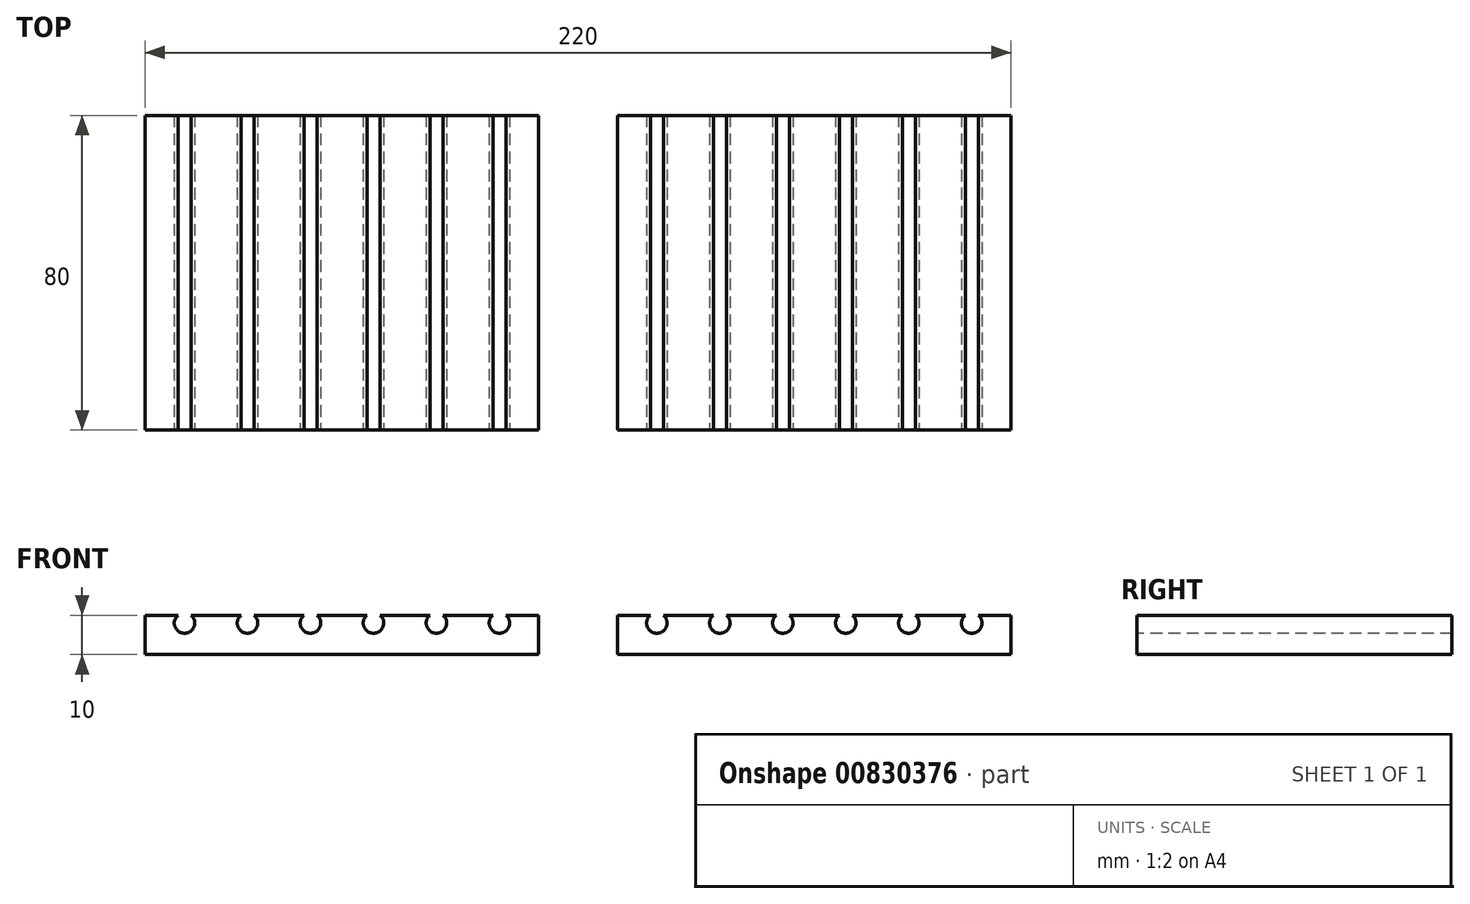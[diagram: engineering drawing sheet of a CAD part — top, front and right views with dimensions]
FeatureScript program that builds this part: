
annotation { "Feature Type Name" : "Feature", "Feature Type Description" : "" }
export const myFeature = defineFeature(function(context is Context, id is Id, definition is map)
    precondition{}
    {
        {
            var Q0;
            Q0=qCreatedBy(makeId("Top.planeOp"),FACE);
            var sketch = newSketch(context, id + "F0", { "sketchPlane" : qUnion([Q0])});
            skLineSegment(sketch, "E0.bottom", {"start": v(50, 40) * mm, "end": v(-50, 40) * mm});
            skLineSegment(sketch, "E0.top", {"start": v(50, -40) * mm, "end": v(-50, -40) * mm});
            skLineSegment(sketch, "E0.left", {"start": v(50, 40) * mm, "end": v(50, -40) * mm});
            skLineSegment(sketch, "E0.right", {"start": v(-50, 40) * mm, "end": v(-50, -40) * mm});
            skPoint(sketch, "E0.middle", {"position": v(0, 0) * mm});
            skSolve(sketch);
        }
        {
            var Q0;
            Q0=makeQuery(id+"F0.imprint","IMPRINT",FACE,{"disambiguationData":[TD([[makeQuery(id+"F0.imprint","IMPRINT",EDGE,{"derivedFrom":sQuery(id+"F0.wireOp",EDGE,"E0.bottom")}),1.0]])]});
            extrude(context, id + "F1", {"entities" : qUnion([Q0]), "depth" : 10 * mm, "offsetDistance" : 25 * mm});
        }
        {
            var Q0;
            Q0=makeQuery(id+"F1.opExtrude","SWEPT_FACE",FACE,{"disambiguationData":[OSD([sQuery(id+"F0.wireOp",EDGE,"E0.top")])]});
            var sketch = newSketch(context, id + "F2", { "sketchPlane" : qUnion([Q0])});
            skLineSegment(sketch, "E1.0.0", {"start": v(-50, 0) * mm, "end": v(50, 0) * mm});
            skLineSegment(sketch, "E1.0.1", {"start": v(50, 0) * mm, "end": v(50, 10) * mm});
            skLineSegment(sketch, "E1.0.2", {"start": v(50, 10) * mm, "end": v(-50, 10) * mm});
            skLineSegment(sketch, "E1.0.3", {"start": v(-50, 10) * mm, "end": v(-50, 0) * mm});
            skLineSegment(sketch, "E2", {"start": v(-50, 8) * mm, "end": v(50, 8) * mm, "construction": true});
            skCircle(sketch, "E3", {"center": v(-40, 8) * mm, "radius": 2.6 * mm});
            skCircle(sketch, "E4.1.0.0", {"center": v(-24, 8) * mm, "radius": 2.6 * mm});
            skCircle(sketch, "E4.2.0.0", {"center": v(-8, 8) * mm, "radius": 2.6 * mm});
            skCircle(sketch, "E4.3.0.0", {"center": v(8, 8) * mm, "radius": 2.6 * mm});
            skCircle(sketch, "E4.4.0.0", {"center": v(24, 8) * mm, "radius": 2.6 * mm});
            skCircle(sketch, "E4.5.0.0", {"center": v(40, 8) * mm, "radius": 2.6 * mm});
            skLineSegment(sketch, "E4.direction1", {"start": v(-40, 8) * mm, "end": v(-24, 8) * mm, "construction": true});
            skSolve(sketch);
        }
        {
            var Q0;
            {var subQ0=sQuery(id+"F2.wireOp",EDGE,"E4.5.0.0");var subQ1=sQuery(id+"F2.wireOp",EDGE,"E1.0.2");var subQ2=makeQuery(id+"F2.imprint","INTERSECT",VERTEX,{"disambiguationData":[OD(0.0)],"derivedFrom":[subQ1,subQ0]});Q0=makeQuery(id+"F2.imprint","IMPRINT",FACE,{"disambiguationData":[TD([[makeQuery(id+"F2.imprint","IMPRINT",EDGE,{"disambiguationData":[TD([[subQ2,-1.0]])],"derivedFrom":subQ1}),-1.0]])]});}
            var Q1;
            {var subQ0=sQuery(id+"F2.wireOp",EDGE,"E4.4.0.0");var subQ1=sQuery(id+"F2.wireOp",EDGE,"E1.0.2");var subQ2=makeQuery(id+"F2.imprint","INTERSECT",VERTEX,{"disambiguationData":[OD(0.0)],"derivedFrom":[subQ1,subQ0]});Q1=makeQuery(id+"F2.imprint","IMPRINT",FACE,{"disambiguationData":[TD([[makeQuery(id+"F2.imprint","IMPRINT",EDGE,{"disambiguationData":[TD([[subQ2,-1.0]])],"derivedFrom":subQ1}),-1.0]])]});}
            var Q2;
            {var subQ0=sQuery(id+"F2.wireOp",EDGE,"E4.3.0.0");var subQ1=sQuery(id+"F2.wireOp",EDGE,"E1.0.2");var subQ2=makeQuery(id+"F2.imprint","INTERSECT",VERTEX,{"disambiguationData":[OD(0.0)],"derivedFrom":[subQ1,subQ0]});Q2=makeQuery(id+"F2.imprint","IMPRINT",FACE,{"disambiguationData":[TD([[makeQuery(id+"F2.imprint","IMPRINT",EDGE,{"disambiguationData":[TD([[subQ2,-1.0]])],"derivedFrom":subQ1}),-1.0]])]});}
            var Q3;
            {var subQ0=sQuery(id+"F2.wireOp",EDGE,"E4.2.0.0");var subQ1=sQuery(id+"F2.wireOp",EDGE,"E1.0.2");var subQ2=makeQuery(id+"F2.imprint","INTERSECT",VERTEX,{"disambiguationData":[OD(0.0)],"derivedFrom":[subQ1,subQ0]});Q3=makeQuery(id+"F2.imprint","IMPRINT",FACE,{"disambiguationData":[TD([[makeQuery(id+"F2.imprint","IMPRINT",EDGE,{"disambiguationData":[TD([[subQ2,-1.0]])],"derivedFrom":subQ1}),-1.0]])]});}
            var Q4;
            {var subQ0=sQuery(id+"F2.wireOp",EDGE,"E4.1.0.0");var subQ1=sQuery(id+"F2.wireOp",EDGE,"E1.0.2");var subQ2=makeQuery(id+"F2.imprint","INTERSECT",VERTEX,{"disambiguationData":[OD(0.0)],"derivedFrom":[subQ1,subQ0]});Q4=makeQuery(id+"F2.imprint","IMPRINT",FACE,{"disambiguationData":[TD([[makeQuery(id+"F2.imprint","IMPRINT",EDGE,{"disambiguationData":[TD([[subQ2,-1.0]])],"derivedFrom":subQ1}),-1.0]])]});}
            var Q5;
            {var subQ0=sQuery(id+"F2.wireOp",EDGE,"E3");var subQ1=sQuery(id+"F2.wireOp",EDGE,"E1.0.2");var subQ2=makeQuery(id+"F2.imprint","INTERSECT",VERTEX,{"disambiguationData":[OD(0.0)],"derivedFrom":[subQ1,subQ0]});Q5=makeQuery(id+"F2.imprint","IMPRINT",FACE,{"disambiguationData":[TD([[makeQuery(id+"F2.imprint","IMPRINT",EDGE,{"disambiguationData":[TD([[subQ2,-1.0]])],"derivedFrom":subQ1}),-1.0]])]});}
            var Q6;
            {var subQ0=sQuery(id+"F2.wireOp",EDGE,"E4.5.0.0");var subQ1=sQuery(id+"F2.wireOp",EDGE,"E1.0.2");var subQ2=makeQuery(id+"F2.imprint","INTERSECT",VERTEX,{"disambiguationData":[OD(0.0)],"derivedFrom":[subQ1,subQ0]});Q6=makeQuery(id+"F2.imprint","IMPRINT",FACE,{"disambiguationData":[TD([[makeQuery(id+"F2.imprint","IMPRINT",EDGE,{"disambiguationData":[TD([[subQ2,-1.0]])],"derivedFrom":subQ1}),1.0]])]});}
            var Q7;
            {var subQ0=sQuery(id+"F2.wireOp",EDGE,"E4.4.0.0");var subQ1=sQuery(id+"F2.wireOp",EDGE,"E1.0.2");var subQ2=makeQuery(id+"F2.imprint","INTERSECT",VERTEX,{"disambiguationData":[OD(0.0)],"derivedFrom":[subQ1,subQ0]});Q7=makeQuery(id+"F2.imprint","IMPRINT",FACE,{"disambiguationData":[TD([[makeQuery(id+"F2.imprint","IMPRINT",EDGE,{"disambiguationData":[TD([[subQ2,-1.0]])],"derivedFrom":subQ1}),1.0]])]});}
            var Q8;
            {var subQ0=sQuery(id+"F2.wireOp",EDGE,"E4.3.0.0");var subQ1=sQuery(id+"F2.wireOp",EDGE,"E1.0.2");var subQ2=makeQuery(id+"F2.imprint","INTERSECT",VERTEX,{"disambiguationData":[OD(0.0)],"derivedFrom":[subQ1,subQ0]});Q8=makeQuery(id+"F2.imprint","IMPRINT",FACE,{"disambiguationData":[TD([[makeQuery(id+"F2.imprint","IMPRINT",EDGE,{"disambiguationData":[TD([[subQ2,-1.0]])],"derivedFrom":subQ1}),1.0]])]});}
            var Q9;
            {var subQ0=sQuery(id+"F2.wireOp",EDGE,"E4.2.0.0");var subQ1=sQuery(id+"F2.wireOp",EDGE,"E1.0.2");var subQ2=makeQuery(id+"F2.imprint","INTERSECT",VERTEX,{"disambiguationData":[OD(0.0)],"derivedFrom":[subQ1,subQ0]});Q9=makeQuery(id+"F2.imprint","IMPRINT",FACE,{"disambiguationData":[TD([[makeQuery(id+"F2.imprint","IMPRINT",EDGE,{"disambiguationData":[TD([[subQ2,-1.0]])],"derivedFrom":subQ1}),1.0]])]});}
            var Q10;
            {var subQ0=sQuery(id+"F2.wireOp",EDGE,"E4.1.0.0");var subQ1=sQuery(id+"F2.wireOp",EDGE,"E1.0.2");var subQ2=makeQuery(id+"F2.imprint","INTERSECT",VERTEX,{"disambiguationData":[OD(0.0)],"derivedFrom":[subQ1,subQ0]});Q10=makeQuery(id+"F2.imprint","IMPRINT",FACE,{"disambiguationData":[TD([[makeQuery(id+"F2.imprint","IMPRINT",EDGE,{"disambiguationData":[TD([[subQ2,-1.0]])],"derivedFrom":subQ1}),1.0]])]});}
            var Q11;
            {var subQ0=sQuery(id+"F2.wireOp",EDGE,"E3");var subQ1=sQuery(id+"F2.wireOp",EDGE,"E1.0.2");var subQ2=makeQuery(id+"F2.imprint","INTERSECT",VERTEX,{"disambiguationData":[OD(0.0)],"derivedFrom":[subQ1,subQ0]});Q11=makeQuery(id+"F2.imprint","IMPRINT",FACE,{"disambiguationData":[TD([[makeQuery(id+"F2.imprint","IMPRINT",EDGE,{"disambiguationData":[TD([[subQ2,-1.0]])],"derivedFrom":subQ1}),1.0]])]});}
            extrude(context, id + "F3", {"entities" : qUnion([Q0, Q1, Q2, Q3, Q4, Q5, Q6, Q7, Q8, Q9, Q10, Q11]), "operationType" : NewBodyOperationType.REMOVE, "endBound" : BoundingType.THROUGH_ALL, "oppositeDirection" : true, "depth" : 25 * mm, "offsetDistance" : 25 * mm});
        }
        {
            var Q0;
            Q0=makeQuery(id+"F1.opExtrude","SWEPT_BODY",BODY,{"disambiguationData":[OSD([sQuery(id+"F0.wireOp",EDGE,"E0.bottom"),sQuery(id+"F0.wireOp",EDGE,"E0.top"),sQuery(id+"F0.wireOp",EDGE,"E0.left"),sQuery(id+"F0.wireOp",EDGE,"E0.right")])]});
            transform(context, id + "F4", {"entities" : qUnion([Q0]), "transformType" : TransformType.TRANSLATION_3D, "dx" : 120 * mm, "dy" : 0 * mm, "dz" : 0 * mm, "makeCopy" : true});
        }
    });
